# Revit family: PRE050004-FR
name_source: partatom
category: Accessoire de canalisation
revit_build: Autodesk Revit 2017 (Build: 20160225_1515(x64)
units: mm (PartAtom-declared; Revit-internal decimal feet)

## family parameters
Basée sur le plan de construction = Non
Cote de connecteur circulaire = Utiliser le diamètre
Couper avec des vides une fois chargée = Non
Partagée = Non
Toujours verticalement = Oui
Type d'élément = Normal

## types (1)
- 31815 PRESTO ROBINET TEMPORISE LAVABO PRESTO 612 AVEC BEC TOURNANT
    Adresse = 7, RUE RACINE - 92542 MONTROUGE CEDEX FRANCE
    Debit = 3 l/min à 3 bars, réglage 4 positions

Dispositif anti-coup de bélier
    Description = Robinet simple temporisé mural (NF) avec bec tournant, alimentation en eau froide. De type Presto 612 réf. 31815 ou techniquement équivalent. Avec mécanisme à rubis auto nettoyé par fil frein, débit préréglé à 3 l/mn. Réglage de débit interne.
    Diamètre Nominal = 15 mm  [stored 0.0492126 ft]
    Fabricant = LES ROBINETS PRESTO S.A.
    Finition = Corps en laiton avec finition chromée
    Flux = 0.1 L/s
    Fonction = Pression d'utilisation recommandée :
- 1 à 5 bars

Débit :
- 3 l/mn à 3 bars - Réglage 4 positions
- Dispositif anti-coup de bélier

Durée d'écoulement :
- 15 secondes ± 5 secondes

Alimentation hydraulique :
- Mâle G 1/2" (15x21) en eau froide

Résistance thermique :
- Ce robinet résiste à une température de 75°C durant 30 minutes dans
  le cadre de chocs thermiques

Sécurité :
- Tête interchangeable et bouton non tournant évitant tout risque
  d'usure prématurée
- Repère par point de couleur inusable et indémontable

Livré avec :
- Notice de pose

Normes / Agréments :
- Classe acoustique II
- Corps en laiton chromé conforme aux normes NF EN1982 / NF EN12164 /
  NF EN12165
- Traitement de surface Nickel-Chrome selon NF EN12540
- Résistance au brouillard salin neutre (NSS) : 200 h selon NF ISO 9227
    Garantie = 10
    HC = 25 mm  [stored 0.082021 ft]
    Hauteur = 171 mm  [stored 0.561024 ft]
    Largeur = 50 mm  [stored 0.164042 ft]
    Lien CCTP = http://www.prestodatashare.com
    Lien fiche produit = http://www.prestodatashare.com
    Lien notice d'utilisation = http://www.prestodatashare.com
    Matériau = Laiton poli chromé
    Modèle = 31815 PRESTO ROBINET TEMPORISE LAVABO PRESTO 612 AVEC BEC TOURNANT
    Perte de charge = 0.0 Pa
    Polantis code = PRE050004-FR
    Pression = 1 à 5 bars
    Profondeur = 190 mm
    Raccordement = Mâle G 1/2" (15x21) en eau froide
    Reference = 31815
    URL = http://www.prestodatashare.com
    URL Fabricant = http://www.prestodatashare.com
    Variantes = 31815

note: [stored X ft] marks values corroborated as IEEE doubles in the binary element streams (Revit-internal decimal feet)
